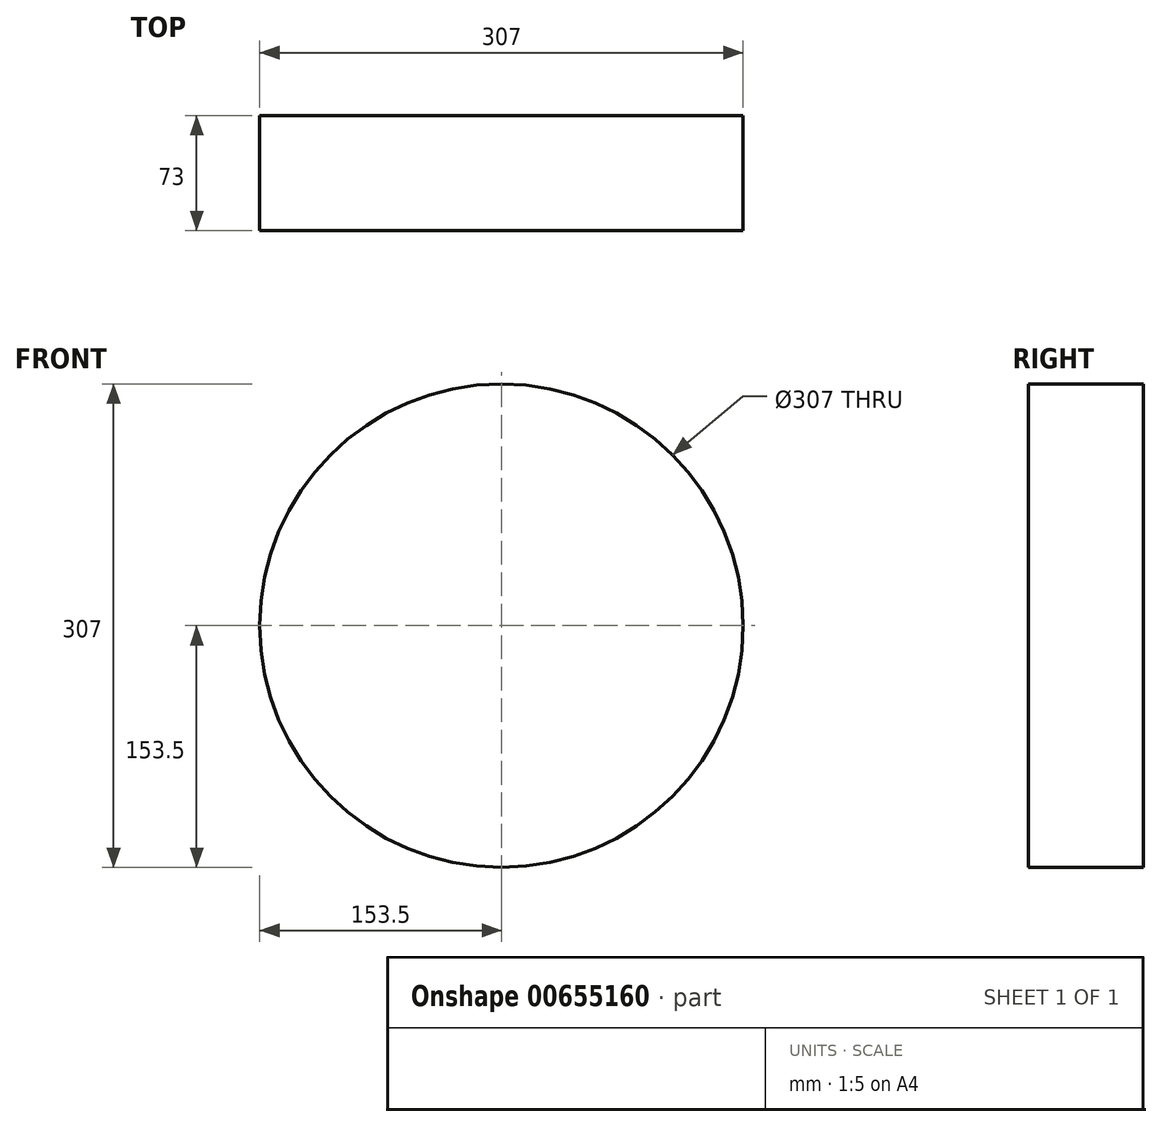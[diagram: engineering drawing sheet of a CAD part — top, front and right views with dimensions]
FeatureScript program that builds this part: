
annotation { "Feature Type Name" : "Feature", "Feature Type Description" : "" }
export const myFeature = defineFeature(function(context is Context, id is Id, definition is map)
    precondition{}
    {
        {
            var Q0;
            Q0=qCreatedBy(makeId("Front.planeOp"),FACE);
            var sketch = newSketch(context, id + "F0", { "sketchPlane" : qUnion([Q0])});
            skCircle(sketch, "E0", {"center": v(0, 0) * mm, "radius": 153.5 * mm});
            skLineSegment(sketch, "E1.bottom", {"start": v(203.5, 203.5) * mm, "end": v(-203.5, 203.5) * mm});
            skLineSegment(sketch, "E1.top", {"start": v(203.5, -203.5) * mm, "end": v(-203.5, -203.5) * mm});
            skLineSegment(sketch, "E1.left", {"start": v(203.5, 203.5) * mm, "end": v(203.5, -203.5) * mm});
            skLineSegment(sketch, "E1.right", {"start": v(-203.5, 203.5) * mm, "end": v(-203.5, -203.5) * mm});
            skSolve(sketch);
        }
        {
            var Q0;
            Q0=sQuery(id+"F0.wireOp",EDGE,"E0");
            extrude(context, id + "F1", {"bodyType" : ToolBodyType.SURFACE, "surfaceEntities" : qUnion([Q0]), "oppositeDirection" : true, "depth" : 73 * mm, "offsetDistance" : 25 * mm});
        }
    });
